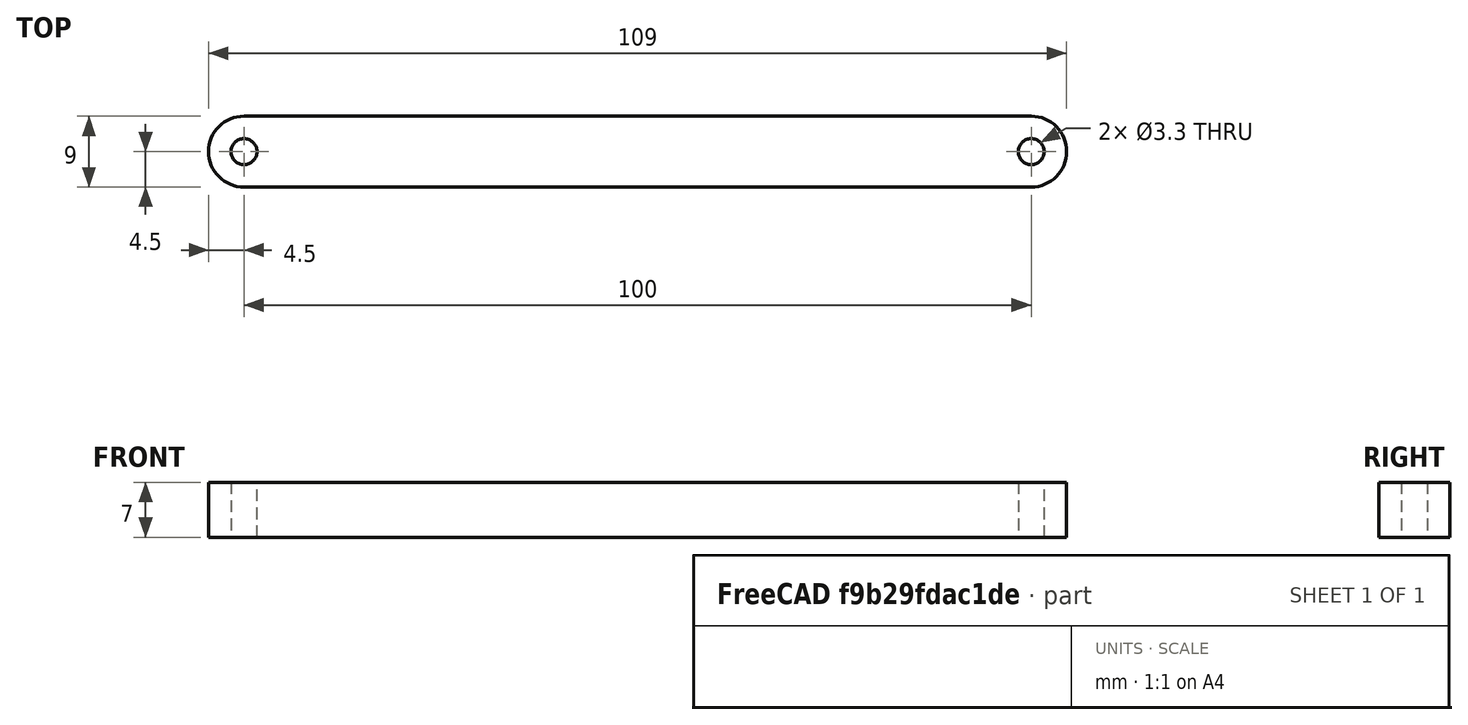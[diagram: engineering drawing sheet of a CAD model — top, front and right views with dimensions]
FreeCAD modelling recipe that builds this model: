
FCSTD DOCUMENT  (FreeCAD 1.1R44874 (Git))
Label: haste-100
License: All rights reserved
LicenseURL: https://en.wikipedia.org/wiki/All_rights_reserved
objects: Sketcher::SketchObject×1, PartDesign::Pad×1, PartDesign::Body×1, App::Point×1
note: 6 computed .brp shape members not serialized (recipe doc carries the construction recipe); baked Part::Feature solids carry a one-line shape summary decoded from their .brp

FEATURE [Sketcher::SketchObject] Sketch
  ArcFitTolerance = 0
  AttachmentSupport = -> [XY_Plane]
  ExternalTypes = [0]
  FullyConstrained = true
  MakeInternals = false
  MapMode = 5
  _ExternalGeoVersion = 0
  sketch-geometry (6):
    g0: ArcOfCircle CenterX=-50 CenterY=0 CenterZ=0 NormalX=0 NormalY=0 NormalZ=1 AngleXU=0 Radius=4.5 StartAngle=1.5708 EndAngle=4.71239
    g1: ArcOfCircle CenterX=50 CenterY=-7e-16 CenterZ=0 NormalX=0 NormalY=0 NormalZ=1 AngleXU=0 Radius=4.5 StartAngle=4.71239 EndAngle=7.85398
    g2: LineSegment StartX=-50 StartY=-4.5 StartZ=0 EndX=50 EndY=-4.5 EndZ=0
    g3: LineSegment StartX=50 StartY=4.5 StartZ=0 EndX=-50 EndY=4.5 EndZ=0
    g4: Circle CenterX=-50 CenterY=0 CenterZ=0 NormalX=0 NormalY=0 NormalZ=1 AngleXU=0 Radius=1.65
    g5: Circle CenterX=50 CenterY=-7e-16 CenterZ=0 NormalX=0 NormalY=0 NormalZ=1 AngleXU=0 Radius=1.65
  constraints (13):
    c: Tangent(g0,g2) = -1.5708
    c: Tangent(g2,g1) = -1.5708
    c: Tangent(g1,g3) = -1.5708
    c: Tangent(g3,g0) = -1.5708
    c: Equal(g0,g1)
    c: Symmetric(g0,g1,g-2)
    c: PointOnObject(g0,g-1)
    c: Radius(g1) = 4.5
    c: DistanceX(g0,g1) = 100
    c: Coincident(g4,g0)
    c: Coincident(g5,g1)
    c: Equal(g5,g4)
    c: Diameter(g5) = 3.3
FEATURE [PartDesign::Pad] Pad
  Direction = (0,0,1)
  Length = 7
  Length2 = 10
  Profile = -> Sketch
  ReferenceAxis = -> Sketch [N_Axis]
  SideType = 0
  Suppressed = false
  Type = 0
  Type2 = 0
FEATURE [PartDesign::Body] Body
  AllowCompound = true
  Group = -> [Sketch,Pad]
  Origin = -> Origin
  Tip = -> Pad
FEATURE [App::Point] Origin001  label="Origem"
  Role = Origin
